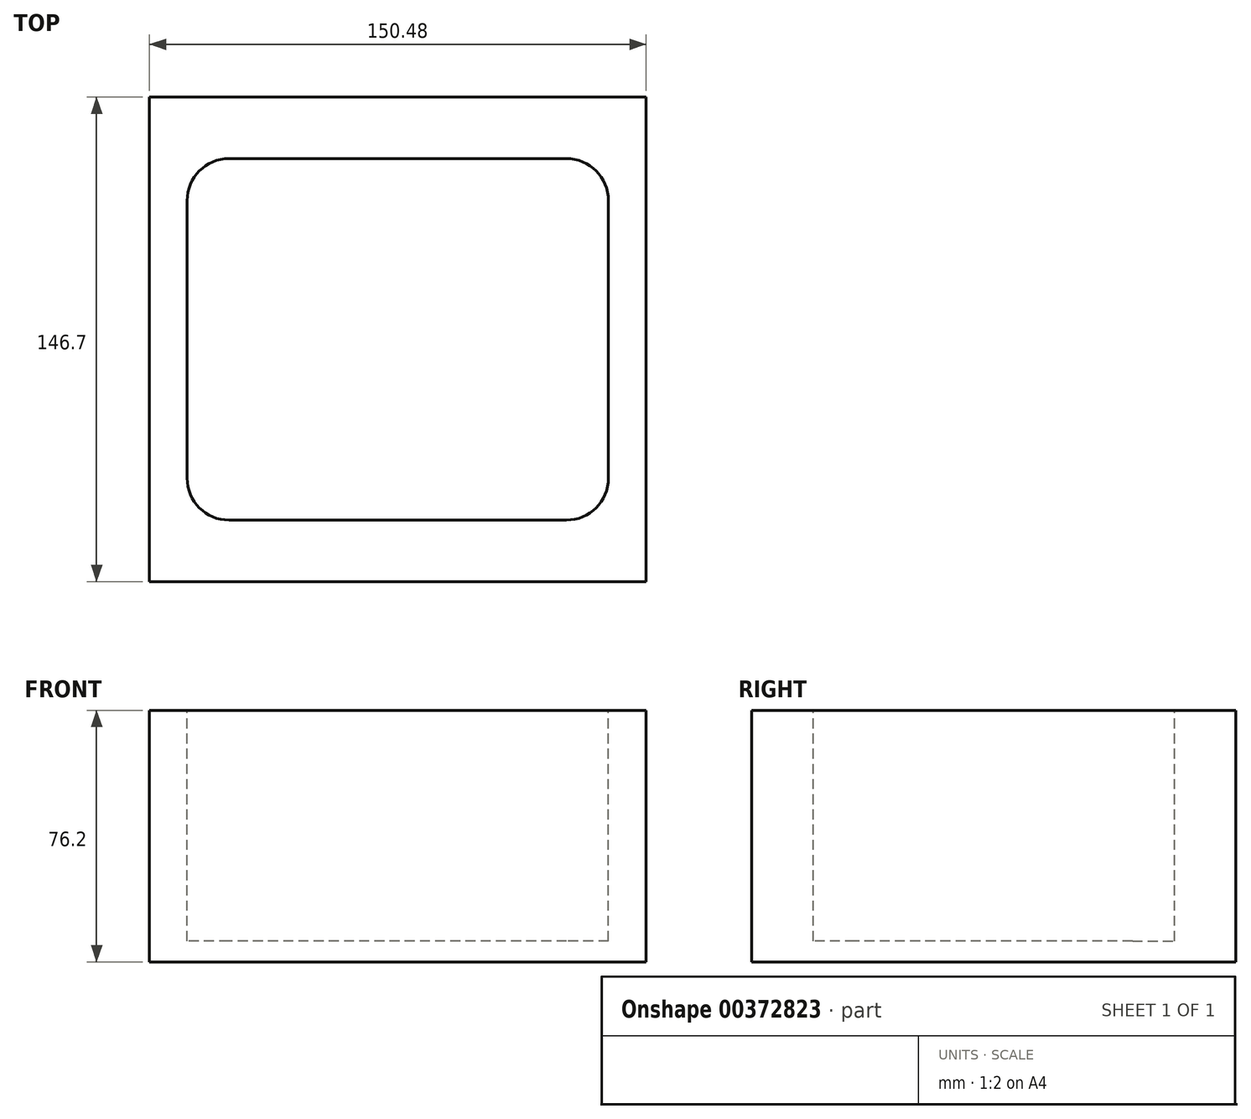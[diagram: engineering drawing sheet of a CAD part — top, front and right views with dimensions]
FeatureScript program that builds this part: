
annotation { "Feature Type Name" : "Feature", "Feature Type Description" : "" }
export const myFeature = defineFeature(function(context is Context, id is Id, definition is map)
    precondition{}
    {
        {
            var Q0;
            Q0=qCreatedBy(makeId("Top.planeOp"),FACE);
            var sketch = newSketch(context, id + "F0", { "sketchPlane" : qUnion([Q0])});
            skLineSegment(sketch, "E0.bottom", {"start": v(75.24, 73.35) * mm, "end": v(-75.24, 73.35) * mm});
            skLineSegment(sketch, "E0.top", {"start": v(75.24, -73.35) * mm, "end": v(-75.24, -73.35) * mm});
            skLineSegment(sketch, "E0.left", {"start": v(75.24, 73.35) * mm, "end": v(75.24, -73.35) * mm});
            skLineSegment(sketch, "E0.right", {"start": v(-75.24, 73.35) * mm, "end": v(-75.24, -73.35) * mm});
            skPoint(sketch, "E0.middle", {"position": v(0, 0) * mm});
            skSolve(sketch);
        }
        {
            var Q0;
            Q0 = qSketchRegion(id + "F0", true);
            extrude(context, id + "F1", {"entities" : qUnion([Q0]), "depth" : 76.2 * mm});
        }
        {
            var Q0;
            Q0=makeQuery(id+"F1.opExtrude","CAP_FACE",FACE,{"disambiguationData":[OSD([sQuery(id+"F0.wireOp",EDGE,"E0.bottom"),sQuery(id+"F0.wireOp",EDGE,"E0.top"),sQuery(id+"F0.wireOp",EDGE,"E0.left"),sQuery(id+"F0.wireOp",EDGE,"E0.right")])],"isStart":false});
            var sketch = newSketch(context, id + "F2", { "sketchPlane" : qUnion([Q0])});
            skLineSegment(sketch, "E1.bottom", {"start": v(63.83, 54.75) * mm, "end": v(-63.83, 54.75) * mm});
            skLineSegment(sketch, "E1.top", {"start": v(63.83, -54.75) * mm, "end": v(-63.83, -54.75) * mm});
            skLineSegment(sketch, "E1.left", {"start": v(63.83, 54.75) * mm, "end": v(63.83, -54.75) * mm});
            skLineSegment(sketch, "E1.right", {"start": v(-63.83, 54.75) * mm, "end": v(-63.83, -54.75) * mm});
            skPoint(sketch, "E1.middle", {"position": v(0, 0) * mm});
            skSolve(sketch);
        }
        {
            var Q0;
            Q0 = qSketchRegion(id + "F2", true);
            extrude(context, id + "F3", {"entities" : qUnion([Q0]), "operationType" : NewBodyOperationType.REMOVE, "oppositeDirection" : true, "depth" : 69.85 * mm});
        }
        {
            var Q0;
            Q0=makeQuery(id+"F3.boolean.opBoolean","COPY",EDGE,{"derivedFrom":makeQuery(id+"F3.opExtrude","SWEPT_EDGE",EDGE,{"disambiguationData":[OSD([sQuery(id+"F2.wireOp",EDGE,"E1.bottom"),sQuery(id+"F2.wireOp",EDGE,"E1.right")])]})});
            var Q1;
            Q1=makeQuery(id+"F3.boolean.opBoolean","COPY",EDGE,{"derivedFrom":makeQuery(id+"F3.opExtrude","SWEPT_EDGE",EDGE,{"disambiguationData":[OSD([sQuery(id+"F2.wireOp",EDGE,"E1.top"),sQuery(id+"F2.wireOp",EDGE,"E1.left")])]})});
            var Q2;
            Q2=makeQuery(id+"F3.boolean.opBoolean","COPY",EDGE,{"derivedFrom":makeQuery(id+"F3.opExtrude","SWEPT_EDGE",EDGE,{"disambiguationData":[OSD([sQuery(id+"F2.wireOp",EDGE,"E1.top"),sQuery(id+"F2.wireOp",EDGE,"E1.right")])]})});
            var Q3;
            Q3=makeQuery(id+"F3.boolean.opBoolean","COPY",EDGE,{"derivedFrom":makeQuery(id+"F3.opExtrude","SWEPT_EDGE",EDGE,{"disambiguationData":[OSD([sQuery(id+"F2.wireOp",EDGE,"E1.bottom"),sQuery(id+"F2.wireOp",EDGE,"E1.left")])]})});
            fillet(context, id + "F4", {"entities" : qUnion([Q0, Q1, Q2, Q3]), "radius" : 12.7 * mm, "tangentPropagation" : true, "allowEdgeOverflow" : false});
        }
    });
